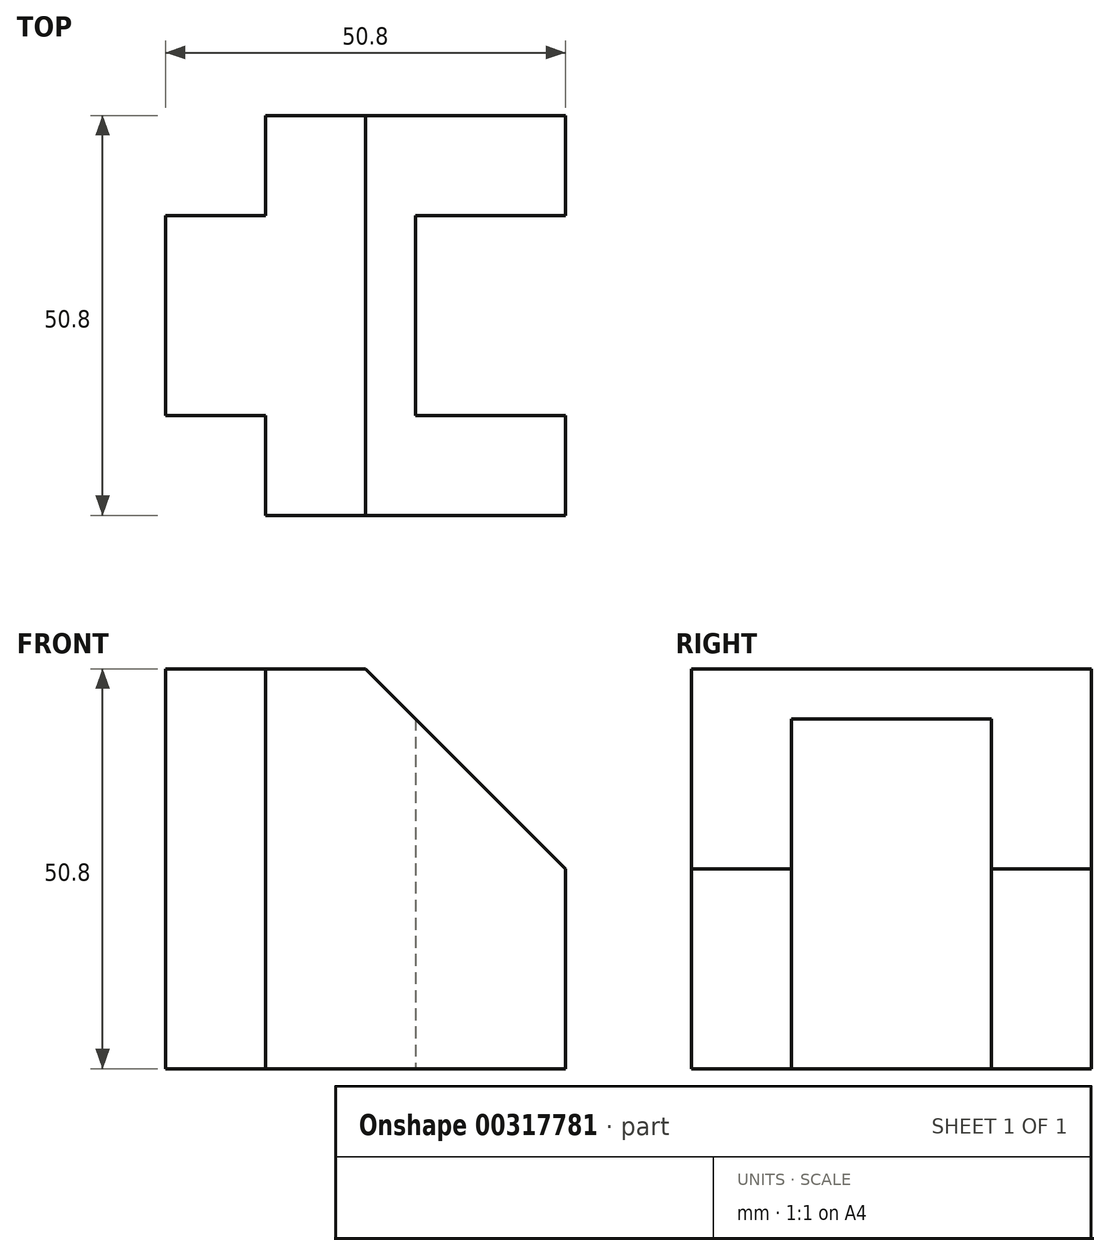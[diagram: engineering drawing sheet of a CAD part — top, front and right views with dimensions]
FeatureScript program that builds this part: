
annotation { "Feature Type Name" : "Feature", "Feature Type Description" : "" }
export const myFeature = defineFeature(function(context is Context, id is Id, definition is map)
    precondition{}
    {
        {
            var Q0;
            Q0=qCreatedBy(makeId("Top.planeOp"),FACE);
            var sketch = newSketch(context, id + "F0", { "sketchPlane" : qUnion([Q0])});
            skLineSegment(sketch, "E0", {"start": v(0, 0) * mm, "end": v(0, 25.4) * mm});
            skLineSegment(sketch, "E1", {"start": v(0, 25.4) * mm, "end": v(12.7, 25.4) * mm});
            skLineSegment(sketch, "E2", {"start": v(12.7, 25.4) * mm, "end": v(12.7, 38.1) * mm});
            skLineSegment(sketch, "E3", {"start": v(12.7, 38.1) * mm, "end": v(50.8, 38.1) * mm});
            skLineSegment(sketch, "E4", {"start": v(50.8, 38.1) * mm, "end": v(50.8, 25.4) * mm});
            skLineSegment(sketch, "E5", {"start": v(50.8, 25.4) * mm, "end": v(31.75, 25.4) * mm});
            skLineSegment(sketch, "E6", {"start": v(31.75, 25.4) * mm, "end": v(31.75, 0) * mm});
            skLineSegment(sketch, "E7", {"start": v(31.75, 0) * mm, "end": v(50.8, 0) * mm});
            skLineSegment(sketch, "E8", {"start": v(50.8, 0) * mm, "end": v(50.8, -12.7) * mm});
            skLineSegment(sketch, "E9", {"start": v(50.8, -12.7) * mm, "end": v(12.7, -12.7) * mm});
            skLineSegment(sketch, "E10", {"start": v(12.7, -12.7) * mm, "end": v(12.7, 0) * mm});
            skLineSegment(sketch, "E11", {"start": v(12.7, 0) * mm, "end": v(0, 0) * mm});
            skLineSegment(sketch, "E12", {"start": v(25.4, 38.1) * mm, "end": v(25.4, -12.7) * mm});
            skSolve(sketch);
        }
        {
            var Q0;
            Q0=makeQuery(id+"F0.imprint","IMPRINT",FACE,{"disambiguationData":[TD([[makeQuery(id+"F0.imprint","IMPRINT",EDGE,{"derivedFrom":sQuery(id+"F0.wireOp",EDGE,"E0")}),-1.0]])]});
            var Q1;
            {var subQ0=sQuery(id+"F0.wireOp",EDGE,"E4");Q1=makeQuery(id+"F0.imprint","IMPRINT",FACE,{"disambiguationData":[TD([[makeQuery(id+"F0.imprint","IMPRINT",EDGE,{"derivedFrom":subQ0}),-1.0]])]});}
            extrude(context, id + "F1", {"entities" : qUnion([Q0, Q1]), "depth" : 50.8 * mm});
        }
        {
            var Q0;
            Q0=makeQuery(id+"F1.opExtrude","SWEPT_FACE",FACE,{"disambiguationData":[OSD([sQuery(id+"F0.wireOp",EDGE,"E9")])]});
            var sketch = newSketch(context, id + "F2", { "sketchPlane" : qUnion([Q0])});
            skLineSegment(sketch, "E13", {"start": v(50.8, 50.8) * mm, "end": v(25.4, 50.8) * mm});
            skLineSegment(sketch, "E14", {"start": v(50.8, 50.8) * mm, "end": v(50.8, 25.4) * mm});
            skLineSegment(sketch, "E15", {"start": v(50.8, 25.4) * mm, "end": v(25.4, 50.8) * mm});
            skSolve(sketch);
        }
        {
            var Q0;
            Q0=makeQuery(id+"F2.imprint","IMPRINT",FACE,{"disambiguationData":[TD([[makeQuery(id+"F2.imprint","IMPRINT",EDGE,{"derivedFrom":sQuery(id+"F2.wireOp",EDGE,"E13")}),1.0]])]});
            extrude(context, id + "F3", {"entities" : qUnion([Q0]), "operationType" : NewBodyOperationType.REMOVE, "endBound" : BoundingType.THROUGH_ALL, "oppositeDirection" : true, "depth" : 25.4 * mm});
        }
    });
